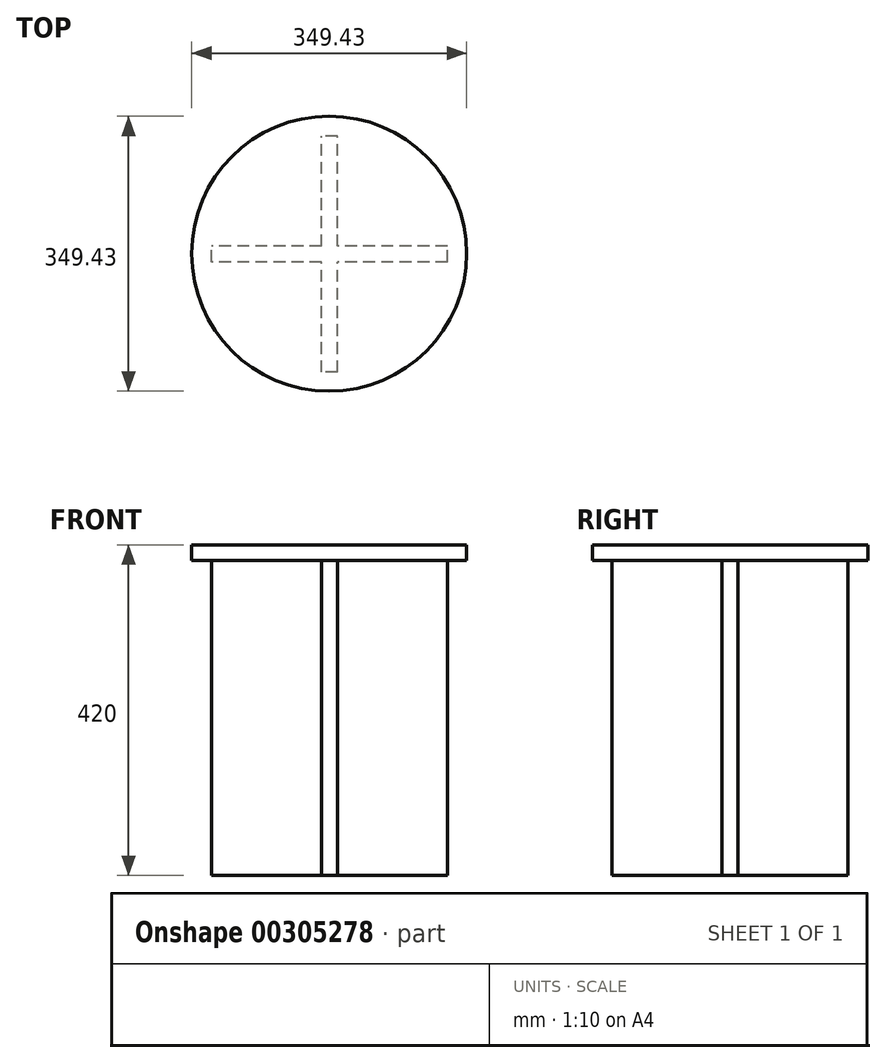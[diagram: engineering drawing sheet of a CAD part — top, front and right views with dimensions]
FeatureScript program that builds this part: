
annotation { "Feature Type Name" : "Feature", "Feature Type Description" : "" }
export const myFeature = defineFeature(function(context is Context, id is Id, definition is map)
    precondition{}
    {
        {
            var Q0;
            Q0=qCreatedBy(makeId("Top.planeOp"),FACE);
            var sketch = newSketch(context, id + "F0", { "sketchPlane" : qUnion([Q0])});
            skLineSegment(sketch, "E0.bottom", {"start": v(150, -10) * mm, "end": v(-150, -10) * mm});
            skLineSegment(sketch, "E0.top", {"start": v(150, 10) * mm, "end": v(-150, 10) * mm});
            skLineSegment(sketch, "E0.left", {"start": v(150, -10) * mm, "end": v(150, 10) * mm});
            skLineSegment(sketch, "E0.right", {"start": v(-150, -10) * mm, "end": v(-150, 10) * mm});
            skPoint(sketch, "E0.middle", {"position": v(0, 0) * mm});
            skLineSegment(sketch, "E1.bottom", {"start": v(10, -150) * mm, "end": v(-10, -150) * mm});
            skLineSegment(sketch, "E1.top", {"start": v(10, 150) * mm, "end": v(-10, 150) * mm});
            skLineSegment(sketch, "E1.left", {"start": v(10, -150) * mm, "end": v(10, 150) * mm});
            skLineSegment(sketch, "E1.right", {"start": v(-10, -150) * mm, "end": v(-10, 150) * mm});
            skSolve(sketch);
        }
        {
            var Q0;
            Q0 = qSketchRegion(id + "F0", true);
            extrude(context, id + "F1", {"entities" : qUnion([Q0]), "depth" : 400 * mm});
        }
        {
            var Q0;
            Q0=makeQuery(id+"F1.opExtrude","CAP_FACE",FACE,{"disambiguationData":[OSD([sQuery(id+"F0.wireOp",EDGE,"E0.bottom"),sQuery(id+"F0.wireOp",EDGE,"E0.top"),sQuery(id+"F0.wireOp",EDGE,"E0.left"),sQuery(id+"F0.wireOp",EDGE,"E0.right"),sQuery(id+"F0.wireOp",EDGE,"E1.bottom"),sQuery(id+"F0.wireOp",EDGE,"E1.top"),sQuery(id+"F0.wireOp",EDGE,"E1.left"),sQuery(id+"F0.wireOp",EDGE,"E1.right")])],"isStart":false});
            var sketch = newSketch(context, id + "F2", { "sketchPlane" : qUnion([Q0])});
            skCircle(sketch, "E2", {"center": v(-0.27, 0.47) * mm, "radius": 174.72 * mm});
            skSolve(sketch);
        }
        {
            var Q0;
            Q0 = qSketchRegion(id + "F2", true);
            extrude(context, id + "F3", {"entities" : qUnion([Q0]), "depth" : 20 * mm});
        }
    });
